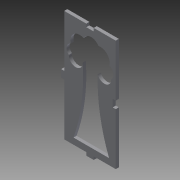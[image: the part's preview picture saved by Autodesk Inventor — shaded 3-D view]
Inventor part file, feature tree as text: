
AUTODESK INVENTOR PART (.ipt)
format: ipt  version: 2015 (Build 190159000, 159)  size: 171,008 bytes
history: native  units: in
note: dims shown in document units (in); Inventor stores cm internally (conversion verified against a paired STEP export)
features: extrude x4, sketch x4
ambient origin geometry x8: Origin, YZ Plane, XZ Plane, XY Plane, X Axis, Y Axis, Z Axis, Center Point
bodies: Solid1 (feature_tree)
feature tree (8):
  extrude  "Extrusion1"  Depth=2.084in
  sketch  "Sketch2"  dims[d2=0.125in d3=0.0in d4=0.15in]
  extrude  "Extrusion2"  Depth=0.125in
  extrude  "Extrusion3"  Depth=0.125in
  sketch  "Sketch3"  dims[d5=0.3in d6=0.125in]
  extrude  "Extrusion4"  Depth=0.3in
  sketch  "Sketch1"  dims[d0=4.5in d1=2.084in]
  sketch  "Sketch4"  dims[d7=0.15in d8=0.3in d9=0.125in d13=0.3in d14=0.15in d15=0.125in d16=0.125in d17=0.0in d18=0.125in d19=0.0in d20=0.3in d21=0.15in d22=0.125in d23=2.8125in d24=0.25in d25=7.0in d26=0.25in d28=7.0in d29=1.041in d30=2.8125in d31=1.0in d32=0.0in]
